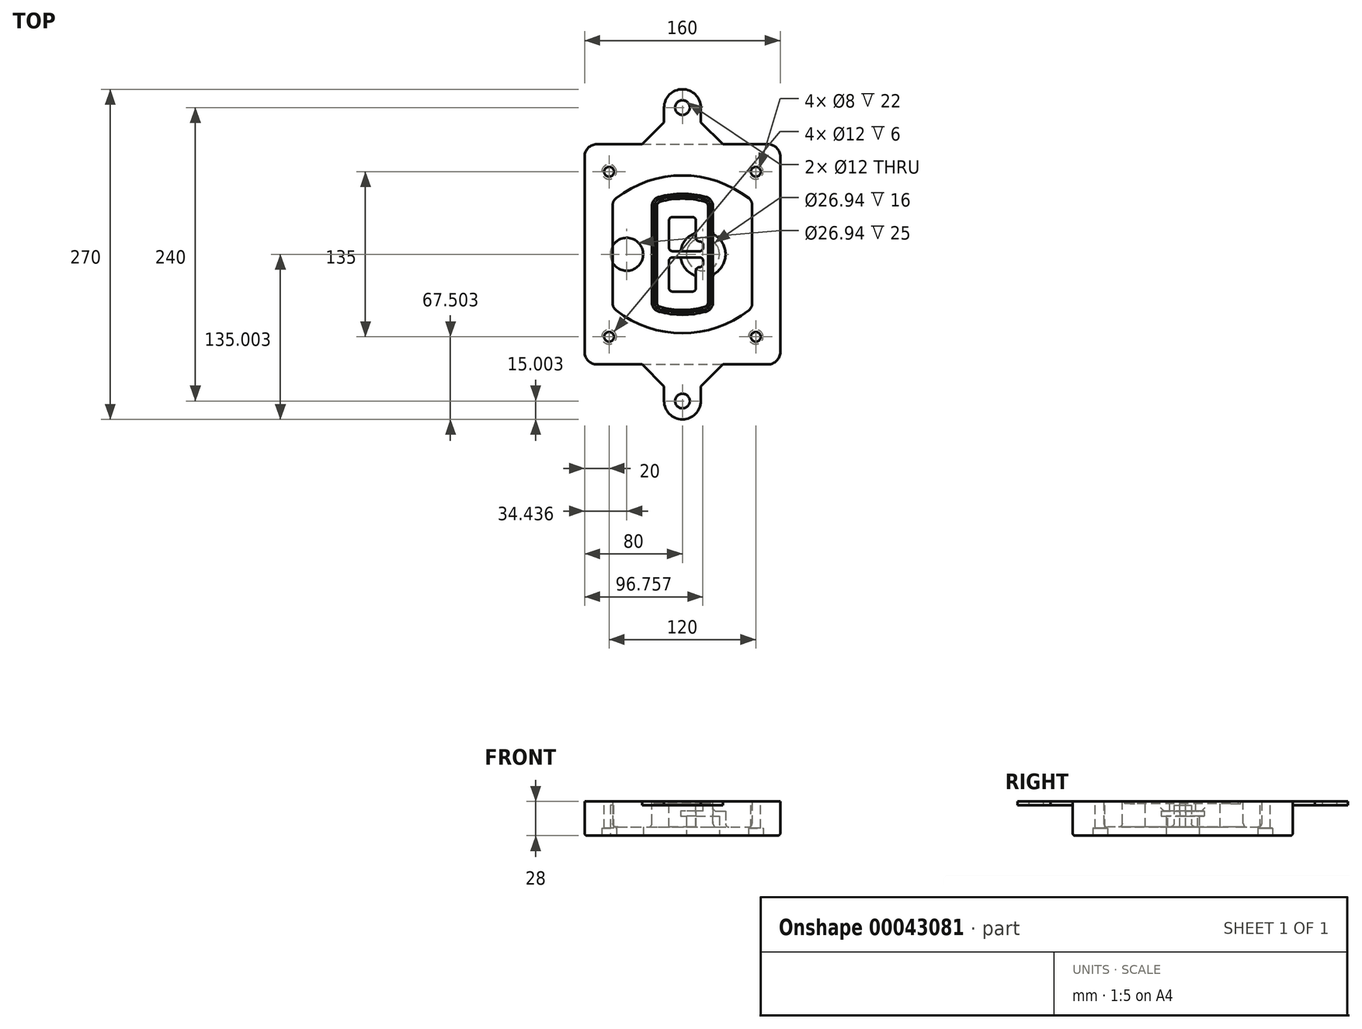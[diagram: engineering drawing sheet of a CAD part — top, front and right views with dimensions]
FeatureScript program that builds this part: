
annotation { "Feature Type Name" : "Feature", "Feature Type Description" : "" }
export const myFeature = defineFeature(function(context is Context, id is Id, definition is map)
    precondition{}
    {
        {
            var Q0;
            Q0=qCreatedBy(makeId("Top.planeOp"),FACE);
            var sketch = newSketch(context, id + "F0", { "sketchPlane" : qUnion([Q0])});
            skPoint(sketch, "E0.rect.middle", {"position": v(0, 0) * mm});
            skLineSegment(sketch, "E1.bottom", {"start": v(24.05, 28.38) * mm, "end": v(164.05, 28.38) * mm});
            skLineSegment(sketch, "E1.top", {"start": v(24.05, 208.38) * mm, "end": v(164.05, 208.38) * mm});
            skLineSegment(sketch, "E1.left", {"start": v(14.05, 38.38) * mm, "end": v(14.05, 198.38) * mm});
            skLineSegment(sketch, "E1.right", {"start": v(174.05, 38.38) * mm, "end": v(174.05, 198.38) * mm});
            skLineSegment(sketch, "E2", {"start": v(14.05, 208.38) * mm, "end": v(174.05, 28.38) * mm, "construction": true});
            skLineSegment(sketch, "E3", {"start": v(174.05, 208.38) * mm, "end": v(14.05, 28.38) * mm, "construction": true});
            skCircle(sketch, "E4", {"center": v(34.05, 185.88) * mm, "radius": 4 * mm});
            skCircle(sketch, "E5", {"center": v(154.05, 185.88) * mm, "radius": 4 * mm});
            skCircle(sketch, "E6", {"center": v(154.05, 50.88) * mm, "radius": 4 * mm});
            skCircle(sketch, "E7", {"center": v(34.05, 50.88) * mm, "radius": 4 * mm});
            skLineSegment(sketch, "E8", {"start": v(34.05, 185.88) * mm, "end": v(154.05, 185.88) * mm, "construction": true});
            skLineSegment(sketch, "E9", {"start": v(154.05, 185.88) * mm, "end": v(154.05, 50.88) * mm, "construction": true});
            skLineSegment(sketch, "E10", {"start": v(154.05, 50.88) * mm, "end": v(34.05, 50.88) * mm, "construction": true});
            skLineSegment(sketch, "E11", {"start": v(34.05, 50.88) * mm, "end": v(34.05, 185.88) * mm, "construction": true});
            skLineSegment(sketch, "E12", {"start": v(34.05, 158.68) * mm, "end": v(34.05, 78.09) * mm});
            skLineSegment(sketch, "E13", {"start": v(154.05, 158.68) * mm, "end": v(154.05, 78.09) * mm});
            skArc(sketch, "E14", {"start": v(150.2, 166.56) * mm, "mid": v(94.05, 185.88) * mm, "end": v(37.9, 166.56) * mm});
            skArc(sketch, "E15", {"start": v(37.9, 70.2) * mm, "mid": v(94.05, 50.88) * mm, "end": v(150.2, 70.2) * mm});
            skLineSegment(sketch, "E16", {"start": v(34.05, 118.38) * mm, "end": v(154.05, 118.38) * mm, "construction": true});
            skPoint(sketch, "E17.visualSharp", {"position": v(34.05, 73.38) * mm});
            skArc(sketch, "E17.filletArc", {"start": v(34.05, 78.09) * mm, "mid": v(35.06, 73.7) * mm, "end": v(37.9, 70.2) * mm});
            skPoint(sketch, "E18.visualSharp", {"position": v(34.05, 163.38) * mm});
            skArc(sketch, "E18.filletArc", {"start": v(37.9, 166.56) * mm, "mid": v(35.06, 163.06) * mm, "end": v(34.05, 158.68) * mm});
            skPoint(sketch, "E19.visualSharp", {"position": v(154.05, 163.38) * mm});
            skArc(sketch, "E19.filletArc", {"start": v(154.05, 158.68) * mm, "mid": v(153.04, 163.06) * mm, "end": v(150.2, 166.56) * mm});
            skPoint(sketch, "E20.visualSharp", {"position": v(154.05, 73.38) * mm});
            skArc(sketch, "E20.filletArc", {"start": v(150.2, 70.2) * mm, "mid": v(153.04, 73.7) * mm, "end": v(154.05, 78.09) * mm});
            skPoint(sketch, "E21.visualSharp", {"position": v(14.05, 208.38) * mm});
            skArc(sketch, "E21.filletArc", {"start": v(24.05, 208.38) * mm, "mid": v(16.98, 205.45) * mm, "end": v(14.05, 198.38) * mm});
            skPoint(sketch, "E22.visualSharp", {"position": v(174.05, 208.38) * mm});
            skArc(sketch, "E22.filletArc", {"start": v(174.05, 198.38) * mm, "mid": v(171.12, 205.45) * mm, "end": v(164.05, 208.38) * mm});
            skPoint(sketch, "E23.visualSharp", {"position": v(174.05, 28.38) * mm});
            skArc(sketch, "E23.filletArc", {"start": v(164.05, 28.38) * mm, "mid": v(171.12, 31.31) * mm, "end": v(174.05, 38.38) * mm});
            skPoint(sketch, "E24.visualSharp", {"position": v(14.05, 28.38) * mm});
            skArc(sketch, "E24.filletArc", {"start": v(14.05, 38.38) * mm, "mid": v(16.98, 31.31) * mm, "end": v(24.05, 28.38) * mm});
            skArc(sketch, "E25.0", {"start": v(151.05, 158.68) * mm, "mid": v(150.34, 161.75) * mm, "end": v(148.36, 164.2) * mm});
            skLineSegment(sketch, "E25.1", {"start": v(151.05, 158.68) * mm, "end": v(151.05, 78.09) * mm});
            skArc(sketch, "E25.2", {"start": v(148.36, 72.57) * mm, "mid": v(150.34, 75.02) * mm, "end": v(151.05, 78.09) * mm});
            skArc(sketch, "E25.3", {"start": v(39.74, 72.57) * mm, "mid": v(94.05, 53.88) * mm, "end": v(148.36, 72.57) * mm});
            skArc(sketch, "E25.4", {"start": v(37.05, 78.09) * mm, "mid": v(37.76, 75.02) * mm, "end": v(39.74, 72.57) * mm});
            skArc(sketch, "E25.5", {"start": v(148.36, 164.2) * mm, "mid": v(94.05, 182.88) * mm, "end": v(39.74, 164.2) * mm});
            skLineSegment(sketch, "E25.6", {"start": v(37.05, 158.68) * mm, "end": v(37.05, 78.09) * mm});
            skArc(sketch, "E25.7", {"start": v(39.74, 164.2) * mm, "mid": v(37.76, 161.75) * mm, "end": v(37.05, 158.68) * mm});
            skArc(sketch, "E26.0", {"start": v(35.43, 169.71) * mm, "mid": v(31.47, 164.82) * mm, "end": v(30.05, 158.68) * mm});
            skArc(sketch, "E26.1", {"start": v(152.67, 169.71) * mm, "mid": v(94.05, 189.88) * mm, "end": v(35.43, 169.71) * mm});
            skArc(sketch, "E26.2", {"start": v(158.05, 158.68) * mm, "mid": v(156.63, 164.82) * mm, "end": v(152.67, 169.71) * mm});
            skLineSegment(sketch, "E26.3", {"start": v(158.05, 158.68) * mm, "end": v(158.05, 78.09) * mm});
            skArc(sketch, "E26.4", {"start": v(152.67, 67.05) * mm, "mid": v(156.63, 71.95) * mm, "end": v(158.05, 78.09) * mm});
            skLineSegment(sketch, "E26.5", {"start": v(30.05, 158.68) * mm, "end": v(30.05, 78.09) * mm});
            skArc(sketch, "E26.6", {"start": v(35.43, 67.05) * mm, "mid": v(94.05, 46.88) * mm, "end": v(152.67, 67.05) * mm});
            skArc(sketch, "E26.7", {"start": v(30.05, 78.09) * mm, "mid": v(31.47, 71.95) * mm, "end": v(35.43, 67.05) * mm});
            skSolve(sketch);
        }
        {
            var Q0;
            Q0=makeQuery(id+"F0.imprint","IMPRINT",FACE,{"disambiguationData":[TD([[makeQuery(id+"F0.imprint","IMPRINT",EDGE,{"derivedFrom":sQuery(id+"F0.wireOp",EDGE,"E1.bottom")}),1.0]])]});
            var Q1;
            Q1=makeQuery(id+"F0.imprint","IMPRINT",FACE,{"disambiguationData":[TD([[makeQuery(id+"F0.imprint","IMPRINT",EDGE,{"derivedFrom":sQuery(id+"F0.wireOp",EDGE,"E12")}),1.0]])]});
            var Q2;
            Q2=makeQuery(id+"F0.imprint","IMPRINT",FACE,{"disambiguationData":[TD([[makeQuery(id+"F0.imprint","IMPRINT",EDGE,{"derivedFrom":sQuery(id+"F0.wireOp",EDGE,"E25.0")}),1.0]])]});
            var Q3;
            Q3=makeQuery(id+"F0.imprint","IMPRINT",FACE,{"disambiguationData":[TD([[makeQuery(id+"F0.imprint","IMPRINT",EDGE,{"derivedFrom":sQuery(id+"F0.wireOp",EDGE,"E12")}),-1.0]])]});
            extrude(context, id + "F1", {"entities" : qUnion([Q0, Q1, Q2, Q3]), "oppositeDirection" : true, "depth" : 25 * mm});
        }
        {
            var Q0;
            Q0=makeQuery(id+"F0.imprint","IMPRINT",FACE,{"disambiguationData":[TD([[makeQuery(id+"F0.imprint","IMPRINT",EDGE,{"derivedFrom":sQuery(id+"F0.wireOp",EDGE,"E12")}),1.0]])]});
            extrude(context, id + "F2", {"entities" : qUnion([Q0]), "operationType" : NewBodyOperationType.ADD, "depth" : 3 * mm});
        }
        {
            var Q0;
            Q0=makeQuery(id+"F0.imprint","IMPRINT",FACE,{"disambiguationData":[TD([[makeQuery(id+"F0.imprint","IMPRINT",EDGE,{"derivedFrom":sQuery(id+"F0.wireOp",EDGE,"E25.0")}),1.0]])]});
            extrude(context, id + "F3", {"entities" : qUnion([Q0]), "operationType" : NewBodyOperationType.REMOVE, "oppositeDirection" : true, "depth" : 18 * mm});
        }
        {
            var Q0;
            Q0=makeQuery(id+"F2.opExtrude","CAP_FACE",FACE,{"disambiguationData":[OSD([sQuery(id+"F0.wireOp",EDGE,"E12"),sQuery(id+"F0.wireOp",EDGE,"E13"),sQuery(id+"F0.wireOp",EDGE,"E14"),sQuery(id+"F0.wireOp",EDGE,"E15"),sQuery(id+"F0.wireOp",EDGE,"E17.filletArc"),sQuery(id+"F0.wireOp",EDGE,"E18.filletArc"),sQuery(id+"F0.wireOp",EDGE,"E19.filletArc"),sQuery(id+"F0.wireOp",EDGE,"E20.filletArc"),sQuery(id+"F0.wireOp",EDGE,"E25.0"),sQuery(id+"F0.wireOp",EDGE,"E25.1"),sQuery(id+"F0.wireOp",EDGE,"E25.2"),sQuery(id+"F0.wireOp",EDGE,"E25.3"),sQuery(id+"F0.wireOp",EDGE,"E25.4"),sQuery(id+"F0.wireOp",EDGE,"E25.5"),sQuery(id+"F0.wireOp",EDGE,"E25.6"),sQuery(id+"F0.wireOp",EDGE,"E25.7")])],"isStart":false});
            var sketch = newSketch(context, id + "F4", { "sketchPlane" : qUnion([Q0])});
            skArc(sketch, "E27.0", {"start": v(74.97, 71.41) * mm, "mid": v(94.05, 68.88) * mm, "end": v(113.13, 71.41) * mm});
            skArc(sketch, "E28.0", {"start": v(113.13, 165.35) * mm, "mid": v(94.05, 167.88) * mm, "end": v(74.97, 165.35) * mm});
            skLineSegment(sketch, "E29", {"start": v(69.05, 157.63) * mm, "end": v(69.05, 79.14) * mm});
            skLineSegment(sketch, "E30", {"start": v(119.05, 157.63) * mm, "end": v(119.05, 79.14) * mm});
            skLineSegment(sketch, "E31", {"start": v(69.05, 163.48) * mm, "end": v(119.05, 163.48) * mm, "construction": true});
            skLineSegment(sketch, "E32", {"start": v(69.05, 73.28) * mm, "end": v(119.05, 73.28) * mm, "construction": true});
            skPoint(sketch, "E33.visualSharp", {"position": v(69.05, 163.48) * mm});
            skArc(sketch, "E33.filletArc", {"start": v(74.97, 165.35) * mm, "mid": v(70.7, 162.5) * mm, "end": v(69.05, 157.63) * mm});
            skPoint(sketch, "E34.visualSharp", {"position": v(119.05, 163.48) * mm});
            skArc(sketch, "E34.filletArc", {"start": v(119.05, 157.63) * mm, "mid": v(117.4, 162.5) * mm, "end": v(113.13, 165.35) * mm});
            skPoint(sketch, "E35.visualSharp", {"position": v(119.05, 73.28) * mm});
            skArc(sketch, "E35.filletArc", {"start": v(113.13, 71.41) * mm, "mid": v(117.4, 74.27) * mm, "end": v(119.05, 79.14) * mm});
            skPoint(sketch, "E36.visualSharp", {"position": v(69.05, 73.28) * mm});
            skArc(sketch, "E36.filletArc", {"start": v(69.05, 79.14) * mm, "mid": v(70.7, 74.27) * mm, "end": v(74.97, 71.41) * mm});
            skArc(sketch, "E37.0", {"start": v(148.36, 164.2) * mm, "mid": v(94.05, 182.88) * mm, "end": v(39.74, 164.2) * mm});
            skArc(sketch, "E37.1", {"start": v(39.74, 164.2) * mm, "mid": v(37.76, 161.75) * mm, "end": v(37.05, 158.68) * mm});
            skLineSegment(sketch, "E37.2", {"start": v(37.05, 158.68) * mm, "end": v(37.05, 78.09) * mm});
            skArc(sketch, "E37.3", {"start": v(37.05, 78.09) * mm, "mid": v(37.76, 75.02) * mm, "end": v(39.74, 72.57) * mm});
            skArc(sketch, "E37.4", {"start": v(39.74, 72.57) * mm, "mid": v(94.05, 53.88) * mm, "end": v(148.36, 72.57) * mm});
            skArc(sketch, "E37.5", {"start": v(148.36, 72.57) * mm, "mid": v(150.34, 75.02) * mm, "end": v(151.05, 78.09) * mm});
            skLineSegment(sketch, "E37.6", {"start": v(151.05, 158.68) * mm, "end": v(151.05, 78.09) * mm});
            skArc(sketch, "E37.7", {"start": v(151.05, 158.68) * mm, "mid": v(150.34, 161.75) * mm, "end": v(148.36, 164.2) * mm});
            skLineSegment(sketch, "E38.0", {"start": v(117.05, 157.63) * mm, "end": v(117.05, 79.14) * mm});
            skArc(sketch, "E38.1", {"start": v(112.61, 73.34) * mm, "mid": v(115.81, 75.49) * mm, "end": v(117.05, 79.14) * mm});
            skArc(sketch, "E38.2", {"start": v(75.49, 73.34) * mm, "mid": v(94.05, 70.88) * mm, "end": v(112.61, 73.34) * mm});
            skArc(sketch, "E38.3", {"start": v(71.05, 79.14) * mm, "mid": v(72.29, 75.49) * mm, "end": v(75.49, 73.34) * mm});
            skLineSegment(sketch, "E38.4", {"start": v(71.05, 157.63) * mm, "end": v(71.05, 79.14) * mm});
            skArc(sketch, "E38.5", {"start": v(117.05, 157.63) * mm, "mid": v(115.81, 161.28) * mm, "end": v(112.61, 163.42) * mm});
            skArc(sketch, "E38.6", {"start": v(75.49, 163.42) * mm, "mid": v(72.29, 161.28) * mm, "end": v(71.05, 157.63) * mm});
            skArc(sketch, "E38.7", {"start": v(112.61, 163.42) * mm, "mid": v(94.05, 165.88) * mm, "end": v(75.49, 163.42) * mm});
            skArc(sketch, "E39.0", {"start": v(115.05, 157.63) * mm, "mid": v(114.23, 160.06) * mm, "end": v(112.1, 161.5) * mm});
            skLineSegment(sketch, "E39.1", {"start": v(115.05, 157.63) * mm, "end": v(115.05, 79.14) * mm});
            skArc(sketch, "E39.2", {"start": v(112.1, 75.27) * mm, "mid": v(114.23, 76.7) * mm, "end": v(115.05, 79.14) * mm});
            skArc(sketch, "E39.3", {"start": v(76, 75.27) * mm, "mid": v(94.05, 72.88) * mm, "end": v(112.1, 75.27) * mm});
            skArc(sketch, "E39.4", {"start": v(73.05, 79.14) * mm, "mid": v(73.87, 76.7) * mm, "end": v(76, 75.27) * mm});
            skArc(sketch, "E39.5", {"start": v(112.1, 161.5) * mm, "mid": v(94.05, 163.88) * mm, "end": v(76, 161.5) * mm});
            skLineSegment(sketch, "E39.6", {"start": v(73.05, 157.63) * mm, "end": v(73.05, 79.14) * mm});
            skArc(sketch, "E39.7", {"start": v(76, 161.5) * mm, "mid": v(73.87, 160.06) * mm, "end": v(73.05, 157.63) * mm});
            skLineSegment(sketch, "E40", {"start": v(69.05, 118.38) * mm, "end": v(119.05, 118.38) * mm, "construction": true});
            skLineSegment(sketch, "E41", {"start": v(83.05, 123.88) * mm, "end": v(83.05, 145.88) * mm});
            skLineSegment(sketch, "E42", {"start": v(86.05, 148.88) * mm, "end": v(102.05, 148.88) * mm});
            skLineSegment(sketch, "E43", {"start": v(105.05, 145.88) * mm, "end": v(105.05, 131.88) * mm});
            skLineSegment(sketch, "E44", {"start": v(108.05, 128.88) * mm, "end": v(108.05, 128.88) * mm});
            skLineSegment(sketch, "E45", {"start": v(111.05, 125.88) * mm, "end": v(111.05, 123.88) * mm});
            skLineSegment(sketch, "E46", {"start": v(108.05, 120.88) * mm, "end": v(86.05, 120.88) * mm});
            skPoint(sketch, "E47.visualSharp", {"position": v(83.05, 148.88) * mm});
            skArc(sketch, "E47.filletArc", {"start": v(86.05, 148.88) * mm, "mid": v(83.93, 148) * mm, "end": v(83.05, 145.88) * mm});
            skPoint(sketch, "E48.visualSharp", {"position": v(105.05, 148.88) * mm});
            skArc(sketch, "E48.filletArc", {"start": v(105.05, 145.88) * mm, "mid": v(104.17, 148) * mm, "end": v(102.05, 148.88) * mm});
            skPoint(sketch, "E49.visualSharp", {"position": v(105.05, 128.88) * mm});
            skArc(sketch, "E49.filletArc", {"start": v(105.05, 131.88) * mm, "mid": v(105.93, 129.76) * mm, "end": v(108.05, 128.88) * mm});
            skPoint(sketch, "E50.visualSharp", {"position": v(111.05, 128.88) * mm});
            skArc(sketch, "E50.filletArc", {"start": v(111.05, 125.88) * mm, "mid": v(110.17, 128) * mm, "end": v(108.05, 128.88) * mm});
            skPoint(sketch, "E51.visualSharp", {"position": v(111.05, 120.88) * mm});
            skArc(sketch, "E51.filletArc", {"start": v(108.05, 120.88) * mm, "mid": v(110.17, 121.76) * mm, "end": v(111.05, 123.88) * mm});
            skPoint(sketch, "E52.visualSharp", {"position": v(83.05, 120.88) * mm});
            skArc(sketch, "E52.filletArc", {"start": v(83.05, 123.88) * mm, "mid": v(83.93, 121.76) * mm, "end": v(86.05, 120.88) * mm});
            skLineSegment(sketch, "E53.0.MirrorCS", {"start": v(108.05, 115.88) * mm, "end": v(86.05, 115.88) * mm});
            skArc(sketch, "E54.0.MirrorCS", {"start": v(83.05, 112.88) * mm, "mid": v(83.93, 115) * mm, "end": v(86.05, 115.88) * mm});
            skLineSegment(sketch, "E55.0.MirrorCS", {"start": v(83.05, 112.88) * mm, "end": v(83.05, 90.88) * mm});
            skArc(sketch, "E56.0.MirrorCS", {"start": v(86.05, 87.88) * mm, "mid": v(83.93, 88.76) * mm, "end": v(83.05, 90.88) * mm});
            skLineSegment(sketch, "E57.0.MirrorCS", {"start": v(86.05, 87.88) * mm, "end": v(102.05, 87.88) * mm});
            skArc(sketch, "E58.0.MirrorCS", {"start": v(105.05, 90.88) * mm, "mid": v(104.17, 88.76) * mm, "end": v(102.05, 87.88) * mm});
            skLineSegment(sketch, "E59.0.MirrorCS", {"start": v(105.05, 90.88) * mm, "end": v(105.05, 104.88) * mm});
            skArc(sketch, "E60.0.MirrorCS", {"start": v(105.05, 104.88) * mm, "mid": v(105.93, 107) * mm, "end": v(108.05, 107.88) * mm});
            skArc(sketch, "E61.0.MirrorCS", {"start": v(111.05, 110.88) * mm, "mid": v(110.17, 108.76) * mm, "end": v(108.05, 107.88) * mm});
            skLineSegment(sketch, "E62.0.MirrorCS", {"start": v(111.05, 110.88) * mm, "end": v(111.05, 112.88) * mm});
            skArc(sketch, "E63.0.MirrorCS", {"start": v(108.05, 115.88) * mm, "mid": v(110.17, 115) * mm, "end": v(111.05, 112.88) * mm});
            skSolve(sketch);
        }
        {
            var Q0;
            Q0=makeQuery(id+"F4.imprint","IMPRINT",FACE,{"disambiguationData":[TD([[makeQuery(id+"F4.imprint","IMPRINT",EDGE,{"derivedFrom":sQuery(id+"F4.wireOp",EDGE,"E27.0")}),1.0]])]});
            var Q1;
            Q1=makeQuery(id+"F4.imprint","IMPRINT",FACE,{"disambiguationData":[TD([[makeQuery(id+"F4.imprint","IMPRINT",EDGE,{"derivedFrom":sQuery(id+"F4.wireOp",EDGE,"E38.0")}),-1.0]])]});
            var Q2;
            Q2=makeQuery(id+"F4.imprint","IMPRINT",FACE,{"disambiguationData":[TD([[makeQuery(id+"F4.imprint","IMPRINT",EDGE,{"derivedFrom":sQuery(id+"F4.wireOp",EDGE,"E39.0")}),1.0]])]});
            extrude(context, id + "F5", {"entities" : qUnion([Q0, Q1, Q2]), "operationType" : NewBodyOperationType.ADD, "endBound" : BoundingType.UP_TO_NEXT, "oppositeDirection" : true, "depth" : 25 * mm});
        }
        {
            var Q0;
            Q0=makeQuery(id+"F4.imprint","IMPRINT",FACE,{"disambiguationData":[TD([[makeQuery(id+"F4.imprint","IMPRINT",EDGE,{"derivedFrom":sQuery(id+"F4.wireOp",EDGE,"E38.0")}),-1.0]])]});
            extrude(context, id + "F6", {"entities" : qUnion([Q0]), "operationType" : NewBodyOperationType.REMOVE, "oppositeDirection" : true, "depth" : 2 * mm});
        }
        {
            var Q0;
            Q0=makeQuery(id+"F1.opExtrude","CAP_FACE",FACE,{"disambiguationData":[OSD([sQuery(id+"F0.wireOp",EDGE,"E1.bottom"),sQuery(id+"F0.wireOp",EDGE,"E1.top"),sQuery(id+"F0.wireOp",EDGE,"E1.left"),sQuery(id+"F0.wireOp",EDGE,"E1.right"),sQuery(id+"F0.wireOp",EDGE,"E4"),sQuery(id+"F0.wireOp",EDGE,"E5"),sQuery(id+"F0.wireOp",EDGE,"E6"),sQuery(id+"F0.wireOp",EDGE,"E7"),sQuery(id+"F0.wireOp",EDGE,"E21.filletArc"),sQuery(id+"F0.wireOp",EDGE,"E22.filletArc"),sQuery(id+"F0.wireOp",EDGE,"E23.filletArc"),sQuery(id+"F0.wireOp",EDGE,"E24.filletArc")])],"isStart":false});
            var sketch = newSketch(context, id + "F7", { "sketchPlane" : qUnion([Q0])});
            skCircle(sketch, "E64", {"center": v(110.8, -118.38) * mm, "radius": 13.47 * mm});
            skCircle(sketch, "E65", {"center": v(48.49, -118.38) * mm, "radius": 13.47 * mm});
            skLineSegment(sketch, "E66", {"start": v(174.05, -118.38) * mm, "end": v(14.05, -118.38) * mm});
            skCircle(sketch, "E67", {"center": v(110.8, -118.38) * mm, "radius": 18.47 * mm});
            skCircle(sketch, "E68", {"center": v(154.05, -185.88) * mm, "radius": 6 * mm});
            skCircle(sketch, "E69", {"center": v(34.05, -185.88) * mm, "radius": 6 * mm});
            skCircle(sketch, "E70", {"center": v(34.05, -50.88) * mm, "radius": 6 * mm});
            skCircle(sketch, "E71", {"center": v(154.05, -50.88) * mm, "radius": 6 * mm});
            skSolve(sketch);
        }
        {
            var Q0;
            {var subQ1=sQuery(id+"F7.wireOp",EDGE,"E66");var subQ4=sQuery(id+"F7.wireOp",EDGE,"E64");var subQ6=makeQuery(id+"F7.imprint","INTERSECT",VERTEX,{"disambiguationData":[OD(0.0)],"derivedFrom":[subQ4,subQ1]});Q0=makeQuery(id+"F7.imprint","IMPRINT",FACE,{"disambiguationData":[TD([[makeQuery(id+"F7.imprint","IMPRINT",EDGE,{"disambiguationData":[TD([[subQ6,-1.0]])],"derivedFrom":subQ4}),-1.0]])]});}
            var Q1;
            {var subQ0=sQuery(id+"F7.wireOp",EDGE,"E66");var subQ1=sQuery(id+"F7.wireOp",EDGE,"E64");var subQ3=makeQuery(id+"F7.imprint","INTERSECT",VERTEX,{"disambiguationData":[OD(0.0)],"derivedFrom":[subQ1,subQ0]});Q1=makeQuery(id+"F7.imprint","IMPRINT",FACE,{"disambiguationData":[TD([[makeQuery(id+"F7.imprint","IMPRINT",EDGE,{"disambiguationData":[TD([[subQ3,-1.0]])],"derivedFrom":subQ1}),1.0]])]});}
            var Q2;
            {var subQ0=sQuery(id+"F7.wireOp",EDGE,"E66");var subQ1=sQuery(id+"F7.wireOp",EDGE,"E64");var subQ3=makeQuery(id+"F7.imprint","INTERSECT",VERTEX,{"disambiguationData":[OD(0.0)],"derivedFrom":[subQ1,subQ0]});Q2=makeQuery(id+"F7.imprint","IMPRINT",FACE,{"disambiguationData":[TD([[makeQuery(id+"F7.imprint","IMPRINT",EDGE,{"disambiguationData":[TD([[subQ3,1.0]])],"derivedFrom":subQ1}),1.0]])]});}
            var Q3;
            {var subQ1=sQuery(id+"F7.wireOp",EDGE,"E66");var subQ4=sQuery(id+"F7.wireOp",EDGE,"E64");var subQ6=makeQuery(id+"F7.imprint","INTERSECT",VERTEX,{"disambiguationData":[OD(0.0)],"derivedFrom":[subQ4,subQ1]});Q3=makeQuery(id+"F7.imprint","IMPRINT",FACE,{"disambiguationData":[TD([[makeQuery(id+"F7.imprint","IMPRINT",EDGE,{"disambiguationData":[TD([[subQ6,1.0]])],"derivedFrom":subQ4}),-1.0]])]});}
            extrude(context, id + "F8", {"entities" : qUnion([Q0, Q1, Q2, Q3]), "operationType" : NewBodyOperationType.ADD, "oppositeDirection" : true, "depth" : 20 * mm});
        }
        {
            var Q0;
            {var subQ0=sQuery(id+"F7.wireOp",EDGE,"E66");var subQ1=sQuery(id+"F7.wireOp",EDGE,"E64");var subQ3=makeQuery(id+"F7.imprint","INTERSECT",VERTEX,{"disambiguationData":[OD(0.0)],"derivedFrom":[subQ1,subQ0]});Q0=makeQuery(id+"F7.imprint","IMPRINT",FACE,{"disambiguationData":[TD([[makeQuery(id+"F7.imprint","IMPRINT",EDGE,{"disambiguationData":[TD([[subQ3,-1.0]])],"derivedFrom":subQ1}),1.0]])]});}
            var Q1;
            {var subQ0=sQuery(id+"F7.wireOp",EDGE,"E66");var subQ1=sQuery(id+"F7.wireOp",EDGE,"E64");var subQ3=makeQuery(id+"F7.imprint","INTERSECT",VERTEX,{"disambiguationData":[OD(0.0)],"derivedFrom":[subQ1,subQ0]});Q1=makeQuery(id+"F7.imprint","IMPRINT",FACE,{"disambiguationData":[TD([[makeQuery(id+"F7.imprint","IMPRINT",EDGE,{"disambiguationData":[TD([[subQ3,1.0]])],"derivedFrom":subQ1}),1.0]])]});}
            extrude(context, id + "F9", {"entities" : qUnion([Q0, Q1]), "operationType" : NewBodyOperationType.REMOVE, "oppositeDirection" : true, "depth" : 16 * mm});
        }
        {
            var Q0;
            {var subQ0=sQuery(id+"F7.wireOp",EDGE,"E66");var subQ1=sQuery(id+"F7.wireOp",EDGE,"E65");var subQ3=makeQuery(id+"F7.imprint","INTERSECT",VERTEX,{"disambiguationData":[OD(0.0)],"derivedFrom":[subQ1,subQ0]});Q0=makeQuery(id+"F7.imprint","IMPRINT",FACE,{"disambiguationData":[TD([[makeQuery(id+"F7.imprint","IMPRINT",EDGE,{"disambiguationData":[TD([[subQ3,-1.0]])],"derivedFrom":subQ1}),1.0]])]});}
            var Q1;
            {var subQ0=sQuery(id+"F7.wireOp",EDGE,"E66");var subQ1=sQuery(id+"F7.wireOp",EDGE,"E65");var subQ3=makeQuery(id+"F7.imprint","INTERSECT",VERTEX,{"disambiguationData":[OD(0.0)],"derivedFrom":[subQ1,subQ0]});Q1=makeQuery(id+"F7.imprint","IMPRINT",FACE,{"disambiguationData":[TD([[makeQuery(id+"F7.imprint","IMPRINT",EDGE,{"disambiguationData":[TD([[subQ3,1.0]])],"derivedFrom":subQ1}),1.0]])]});}
            extrude(context, id + "F10", {"entities" : qUnion([Q0, Q1]), "operationType" : NewBodyOperationType.REMOVE, "oppositeDirection" : true, "depth" : 25 * mm});
        }
        {
            var Q0;
            Q0=makeQuery(id+"F7.imprint","IMPRINT",FACE,{"disambiguationData":[TD([[makeQuery(id+"F7.imprint","IMPRINT",EDGE,{"derivedFrom":sQuery(id+"F7.wireOp",EDGE,"E68")}),1.0]])]});
            var Q1;
            Q1=makeQuery(id+"F7.imprint","IMPRINT",FACE,{"disambiguationData":[TD([[makeQuery(id+"F7.imprint","IMPRINT",EDGE,{"derivedFrom":makeQuery(id+"F1.opExtrude","CAP_EDGE",EDGE,{"disambiguationData":[OSD([sQuery(id+"F0.wireOp",EDGE,"E5")])],"isStart":false})}),-1.0]])]});
            var Q2;
            Q2=makeQuery(id+"F7.imprint","IMPRINT",FACE,{"disambiguationData":[TD([[makeQuery(id+"F7.imprint","IMPRINT",EDGE,{"derivedFrom":sQuery(id+"F7.wireOp",EDGE,"E69")}),1.0]])]});
            var Q3;
            Q3=makeQuery(id+"F7.imprint","IMPRINT",FACE,{"disambiguationData":[TD([[makeQuery(id+"F7.imprint","IMPRINT",EDGE,{"derivedFrom":makeQuery(id+"F1.opExtrude","CAP_EDGE",EDGE,{"disambiguationData":[OSD([sQuery(id+"F0.wireOp",EDGE,"E4")])],"isStart":false})}),-1.0]])]});
            var Q4;
            Q4=makeQuery(id+"F7.imprint","IMPRINT",FACE,{"disambiguationData":[TD([[makeQuery(id+"F7.imprint","IMPRINT",EDGE,{"derivedFrom":sQuery(id+"F7.wireOp",EDGE,"E70")}),1.0]])]});
            var Q5;
            Q5=makeQuery(id+"F7.imprint","IMPRINT",FACE,{"disambiguationData":[TD([[makeQuery(id+"F7.imprint","IMPRINT",EDGE,{"derivedFrom":makeQuery(id+"F1.opExtrude","CAP_EDGE",EDGE,{"disambiguationData":[OSD([sQuery(id+"F0.wireOp",EDGE,"E7")])],"isStart":false})}),-1.0]])]});
            var Q6;
            Q6=makeQuery(id+"F7.imprint","IMPRINT",FACE,{"disambiguationData":[TD([[makeQuery(id+"F7.imprint","IMPRINT",EDGE,{"derivedFrom":sQuery(id+"F7.wireOp",EDGE,"E71")}),1.0]])]});
            var Q7;
            Q7=makeQuery(id+"F7.imprint","IMPRINT",FACE,{"disambiguationData":[TD([[makeQuery(id+"F7.imprint","IMPRINT",EDGE,{"derivedFrom":makeQuery(id+"F1.opExtrude","CAP_EDGE",EDGE,{"disambiguationData":[OSD([sQuery(id+"F0.wireOp",EDGE,"E6")])],"isStart":false})}),-1.0]])]});
            extrude(context, id + "F11", {"entities" : qUnion([Q0, Q1, Q2, Q3, Q4, Q5, Q6, Q7]), "operationType" : NewBodyOperationType.REMOVE, "oppositeDirection" : true, "depth" : 6 * mm});
        }
        {
            var Q0;
            Q0=makeQuery(id+"F9.boolean.opBoolean","COPY",FACE,{"derivedFrom":makeQuery(id+"F9.opExtrude","CAP_FACE",FACE,{"disambiguationData":[OSD([sQuery(id+"F7.wireOp",EDGE,"E64")])],"isStart":false})});
            var sketch = newSketch(context, id + "F12", { "sketchPlane" : qUnion([Q0])});
            skArc(sketch, "E72.0", {"start": v(105.05, -100.83) * mm, "mid": v(96.62, -106.56) * mm, "end": v(92.5, -115.88) * mm});
            skArc(sketch, "E72.1", {"start": v(92.5, -120.88) * mm, "mid": v(96.62, -130.2) * mm, "end": v(105.05, -135.93) * mm});
            skLineSegment(sketch, "E73", {"start": v(92.5, -120.88) * mm, "end": v(108.05, -120.88) * mm});
            skLineSegment(sketch, "E74.0", {"start": v(108.05, -115.88) * mm, "end": v(92.5, -115.88) * mm});
            skArc(sketch, "E74.1", {"start": v(108.05, -115.88) * mm, "mid": v(110.17, -115) * mm, "end": v(111.05, -112.88) * mm});
            skLineSegment(sketch, "E74.2", {"start": v(111.05, -110.88) * mm, "end": v(111.05, -112.88) * mm});
            skArc(sketch, "E74.3", {"start": v(111.05, -110.88) * mm, "mid": v(110.17, -108.76) * mm, "end": v(108.05, -107.88) * mm});
            skArc(sketch, "E74.4", {"start": v(105.05, -104.88) * mm, "mid": v(105.93, -107) * mm, "end": v(108.05, -107.88) * mm});
            skLineSegment(sketch, "E74.5", {"start": v(105.05, -100.83) * mm, "end": v(105.05, -104.88) * mm});
            skLineSegment(sketch, "E74.7", {"start": v(108.05, -120.88) * mm, "end": v(92.5, -120.88) * mm});
            skArc(sketch, "E74.8", {"start": v(108.05, -120.88) * mm, "mid": v(110.17, -121.76) * mm, "end": v(111.05, -123.88) * mm});
            skLineSegment(sketch, "E74.9", {"start": v(111.05, -125.88) * mm, "end": v(111.05, -123.88) * mm});
            skArc(sketch, "E74.10", {"start": v(111.05, -125.88) * mm, "mid": v(110.17, -128) * mm, "end": v(108.05, -128.88) * mm});
            skArc(sketch, "E74.11", {"start": v(105.05, -131.88) * mm, "mid": v(105.93, -129.76) * mm, "end": v(108.05, -128.88) * mm});
            skLineSegment(sketch, "E74.12", {"start": v(105.05, -135.93) * mm, "end": v(105.05, -131.88) * mm});
            skPoint(sketch, "E75.orphan", {"position": v(105.05, -145.88) * mm});
            skPoint(sketch, "E76.orphan", {"position": v(86.05, -120.88) * mm});
            skPoint(sketch, "E77.orphan", {"position": v(86.05, -115.88) * mm});
            skPoint(sketch, "E78.orphan", {"position": v(105.05, -90.88) * mm});
            skSolve(sketch);
        }
        {
            var Q0;
            {var subQ7=sQuery(id+"F12.wireOp",EDGE,"E72.0");var subQ14=sQuery(id+"F12.wireOp",EDGE,"E72.1");var subQ16=sQuery(id+"F12.wireOp",EDGE,"E74.1");var subQ18=sQuery(id+"F12.wireOp",EDGE,"E74.8");Q0=qUnion([makeQuery(id+"F12.imprint","IMPRINT",FACE,{"disambiguationData":[TD([[makeQuery(id+"F12.imprint","IMPRINT",EDGE,{"derivedFrom":subQ7}),1.0]])]}),makeQuery(id+"F12.imprint","IMPRINT",FACE,{"disambiguationData":[TD([[makeQuery(id+"F12.imprint","IMPRINT",EDGE,{"derivedFrom":subQ14}),1.0]])]}),makeQuery(id+"F12.imprint","IMPRINT",FACE,{"disambiguationData":[TD([[makeQuery(id+"F12.imprint","IMPRINT",EDGE,{"derivedFrom":subQ16}),1.0]])]}),makeQuery(id+"F12.imprint","IMPRINT",FACE,{"disambiguationData":[TD([[makeQuery(id+"F12.imprint","IMPRINT",EDGE,{"derivedFrom":subQ18}),-1.0]])]})]);}
            var Q1;
            Q1=makeQuery(id+"F5.boolean.opBoolean","SPLIT",FACE,{"disambiguationData":[TD([makeQuery(id+"F5.opExtrude","SWEPT_FACE",FACE,{"disambiguationData":[OSD([sQuery(id+"F4.wireOp",EDGE,"E41")])]})])],"derivedFrom":makeQuery(id+"F3.boolean.opBoolean","COPY",FACE,{"derivedFrom":makeQuery(id+"F3.opExtrude","CAP_FACE",FACE,{"disambiguationData":[OSD([sQuery(id+"F0.wireOp",EDGE,"E25.0"),sQuery(id+"F0.wireOp",EDGE,"E25.1"),sQuery(id+"F0.wireOp",EDGE,"E25.2"),sQuery(id+"F0.wireOp",EDGE,"E25.3"),sQuery(id+"F0.wireOp",EDGE,"E25.4"),sQuery(id+"F0.wireOp",EDGE,"E25.5"),sQuery(id+"F0.wireOp",EDGE,"E25.6"),sQuery(id+"F0.wireOp",EDGE,"E25.7")])],"isStart":false})})});
            extrude(context, id + "F13", {"entities" : qUnion([Q0]), "operationType" : NewBodyOperationType.REMOVE, "endBound" : BoundingType.UP_TO_SURFACE, "endBoundEntityFace" : qUnion([Q1]), "depth" : 25 * mm});
        }
        {
            var Q0;
            Q0=makeQuery(id+"F3.boolean.opBoolean","COPY",EDGE,{"derivedFrom":makeQuery(id+"F3.opExtrude","CAP_EDGE",EDGE,{"disambiguationData":[OSD([sQuery(id+"F0.wireOp",EDGE,"E25.6")])],"isStart":false})});
            var Q1;
            Q1=makeQuery(id+"F8.boolean.opBoolean","INTERSECT",EDGE,{"derivedFrom":[makeQuery(id+"F5.opExtrude","SWEPT_FACE",FACE,{"disambiguationData":[OSD([sQuery(id+"F4.wireOp",EDGE,"E30")])]}),makeQuery(id+"F8.opExtrude","CAP_FACE",FACE,{"disambiguationData":[OSD([sQuery(id+"F7.wireOp",EDGE,"E67")])],"isStart":false})]});
            var Q2;
            Q2=makeQuery(id+"F8.boolean.opBoolean","INTERSECT",EDGE,{"disambiguationData":[OD(1.0)],"derivedFrom":[makeQuery(id+"F5.opExtrude","SWEPT_FACE",FACE,{"disambiguationData":[OSD([sQuery(id+"F4.wireOp",EDGE,"E30")])]}),makeQuery(id+"F8.opExtrude","SWEPT_FACE",FACE,{"disambiguationData":[OSD([sQuery(id+"F7.wireOp",EDGE,"E67")])]})]});
            var Q3;
            {var subQ0=sQuery(id+"F4.wireOp",EDGE,"E30");Q3=makeQuery(id+"F8.boolean.opBoolean","SPLIT",EDGE,{"disambiguationData":[TD([makeQuery(id+"F5.opExtrude","SWEPT_FACE",FACE,{"disambiguationData":[OSD([sQuery(id+"F4.wireOp",EDGE,"E35.filletArc")])]})])],"derivedFrom":makeQuery(id+"F5.opExtrude","CAP_EDGE",EDGE,{"disambiguationData":[OSD([subQ0])],"isStart":false})});}
            var Q4;
            {var subQ0=sQuery(id+"F0.wireOp",EDGE,"E25.7");var subQ1=sQuery(id+"F0.wireOp",EDGE,"E25.1");var subQ2=sQuery(id+"F0.wireOp",EDGE,"E25.6");var subQ3=sQuery(id+"F0.wireOp",EDGE,"E25.5");var subQ4=sQuery(id+"F0.wireOp",EDGE,"E25.4");var subQ5=sQuery(id+"F0.wireOp",EDGE,"E25.0");var subQ6=sQuery(id+"F0.wireOp",EDGE,"E25.2");var subQ7=sQuery(id+"F0.wireOp",EDGE,"E25.3");Q4=makeQuery(id+"F8.boolean.opBoolean","INTERSECT",EDGE,{"derivedFrom":[makeQuery(id+"F5.boolean.opBoolean","SPLIT",FACE,{"disambiguationData":[TD([makeQuery(id+"F2.opExtrude","SWEPT_FACE",FACE,{"disambiguationData":[OSD([subQ5])]})])],"derivedFrom":makeQuery(id+"F3.boolean.opBoolean","COPY",FACE,{"derivedFrom":makeQuery(id+"F3.opExtrude","CAP_FACE",FACE,{"disambiguationData":[OSD([subQ5,subQ1,subQ6,subQ7,subQ4,subQ3,subQ2,subQ0])],"isStart":false})})}),makeQuery(id+"F8.opExtrude","SWEPT_FACE",FACE,{"disambiguationData":[OSD([sQuery(id+"F7.wireOp",EDGE,"E67")])]})]});}
            var Q5;
            Q5=makeQuery(id+"F8.boolean.opBoolean","INTERSECT",EDGE,{"disambiguationData":[OD(0.0)],"derivedFrom":[makeQuery(id+"F5.opExtrude","SWEPT_FACE",FACE,{"disambiguationData":[OSD([sQuery(id+"F4.wireOp",EDGE,"E30")])]}),makeQuery(id+"F8.opExtrude","SWEPT_FACE",FACE,{"disambiguationData":[OSD([sQuery(id+"F7.wireOp",EDGE,"E67")])]})]});
            fillet(context, id + "F14", {"entities" : qUnion([Q0, Q1, Q2, Q3, Q4, Q5]), "radius" : 3 * mm, "tangentPropagation" : true, "allowEdgeOverflow" : false});
        }
        {
            var Q0;
            Q0=makeQuery(id+"F1.opExtrude","CAP_EDGE",EDGE,{"disambiguationData":[OSD([sQuery(id+"F0.wireOp",EDGE,"E1.bottom")])],"isStart":false});
            fillet(context, id + "F15", {"entities" : qUnion([Q0]), "radius" : 2 * mm, "tangentPropagation" : true, "allowEdgeOverflow" : false});
        }
        {
            var Q0;
            {var subQ0=sQuery(id+"F0.wireOp",EDGE,"E1.bottom");var subQ1=sQuery(id+"F0.wireOp",EDGE,"E1.top");var subQ2=sQuery(id+"F0.wireOp",EDGE,"E1.left");var subQ3=sQuery(id+"F0.wireOp",EDGE,"E1.right");var subQ4=sQuery(id+"F0.wireOp",EDGE,"E4");var subQ5=sQuery(id+"F0.wireOp",EDGE,"E5");var subQ6=sQuery(id+"F0.wireOp",EDGE,"E6");var subQ7=sQuery(id+"F0.wireOp",EDGE,"E7");var subQ8=sQuery(id+"F0.wireOp",EDGE,"E21.filletArc");var subQ9=sQuery(id+"F0.wireOp",EDGE,"E22.filletArc");var subQ10=sQuery(id+"F0.wireOp",EDGE,"E23.filletArc");var subQ11=sQuery(id+"F0.wireOp",EDGE,"E24.filletArc");Q0=makeQuery(id+"F2.boolean.opBoolean","SPLIT",FACE,{"disambiguationData":[TD([makeQuery(id+"F1.opExtrude","SWEPT_FACE",FACE,{"disambiguationData":[OSD([subQ0])]})])],"derivedFrom":makeQuery(id+"F1.opExtrude","CAP_FACE",FACE,{"disambiguationData":[OSD([subQ0,subQ1,subQ2,subQ3,subQ4,subQ5,subQ6,subQ7,subQ8,subQ9,subQ10,subQ11])],"isStart":true})});}
            var sketch = newSketch(context, id + "F16", { "sketchPlane" : qUnion([Q0])});
            skLineSegment(sketch, "E79", {"start": v(94.05, 208.38) * mm, "end": v(94.05, 238.38) * mm, "construction": true});
            skPoint(sketch, "E79.endSnap0", {"position": v(94.05, 208.38) * mm});
            skCircle(sketch, "E80", {"center": v(94.05, 238.38) * mm, "radius": 6 * mm});
            skArc(sketch, "E81", {"start": v(109.05, 238.38) * mm, "mid": v(94.05, 253.38) * mm, "end": v(79.05, 238.38) * mm});
            skLineSegment(sketch, "E82", {"start": v(79.05, 238.38) * mm, "end": v(79.05, 226.38) * mm});
            skLineSegment(sketch, "E83", {"start": v(79.05, 226.38) * mm, "end": v(61.05, 208.38) * mm});
            skLineSegment(sketch, "E84", {"start": v(109.05, 238.38) * mm, "end": v(109.05, 226.38) * mm});
            skLineSegment(sketch, "E85", {"start": v(109.05, 226.38) * mm, "end": v(127.05, 208.38) * mm});
            skLineSegment(sketch, "E86", {"start": v(14.05, 118.38) * mm, "end": v(174.05, 118.38) * mm, "construction": true});
            skLineSegment(sketch, "E87.MirrorCS", {"start": v(109.05, 10.38) * mm, "end": v(127.05, 28.38) * mm});
            skLineSegment(sketch, "E88.MirrorCS", {"start": v(79.05, 10.38) * mm, "end": v(61.05, 28.38) * mm});
            skArc(sketch, "E89.MirrorCS", {"start": v(109.05, -1.62) * mm, "mid": v(94.05, -16.62) * mm, "end": v(79.05, -1.62) * mm});
            skLineSegment(sketch, "E90.MirrorCS", {"start": v(79.05, -1.62) * mm, "end": v(79.05, 10.38) * mm});
            skLineSegment(sketch, "E91.MirrorCS", {"start": v(109.05, -1.62) * mm, "end": v(109.05, 10.38) * mm});
            skCircle(sketch, "E92.MirrorC", {"center": v(94.05, -1.62) * mm, "radius": 6 * mm});
            skLineSegment(sketch, "E93.MirrorCS", {"start": v(94.05, 28.38) * mm, "end": v(94.05, -1.62) * mm, "construction": true});
            skSolve(sketch);
        }
        {
            var Q0;
            Q0=makeQuery(id+"F16.imprint","IMPRINT",FACE,{"disambiguationData":[TD([[makeQuery(id+"F16.imprint","IMPRINT",EDGE,{"derivedFrom":sQuery(id+"F16.wireOp",EDGE,"E80")}),-1.0]])]});
            var Q1;
            {var subQ1=sQuery(id+"F16.wireOp",EDGE,"E87.MirrorCS");Q1=makeQuery(id+"F16.imprint","IMPRINT",FACE,{"disambiguationData":[TD([[makeQuery(id+"F16.imprint","IMPRINT",EDGE,{"derivedFrom":subQ1}),1.0]])]});}
            var Q2;
            Q2=makeQuery(id+"F16.imprint","IMPRINT",FACE,{"disambiguationData":[TD([[makeQuery(id+"F16.imprint","IMPRINT",EDGE,{"derivedFrom":makeQuery(id+"F1.opExtrude","CAP_EDGE",EDGE,{"disambiguationData":[OSD([sQuery(id+"F0.wireOp",EDGE,"E1.left")])],"isStart":true})}),-1.0]])]});
            var Q3;
            Q3=makeQuery(id+"F2.opExtrude","CAP_FACE",FACE,{"disambiguationData":[OSD([sQuery(id+"F0.wireOp",EDGE,"E12"),sQuery(id+"F0.wireOp",EDGE,"E13"),sQuery(id+"F0.wireOp",EDGE,"E14"),sQuery(id+"F0.wireOp",EDGE,"E15"),sQuery(id+"F0.wireOp",EDGE,"E17.filletArc"),sQuery(id+"F0.wireOp",EDGE,"E18.filletArc"),sQuery(id+"F0.wireOp",EDGE,"E19.filletArc"),sQuery(id+"F0.wireOp",EDGE,"E20.filletArc"),sQuery(id+"F0.wireOp",EDGE,"E25.0"),sQuery(id+"F0.wireOp",EDGE,"E25.1"),sQuery(id+"F0.wireOp",EDGE,"E25.2"),sQuery(id+"F0.wireOp",EDGE,"E25.3"),sQuery(id+"F0.wireOp",EDGE,"E25.4"),sQuery(id+"F0.wireOp",EDGE,"E25.5"),sQuery(id+"F0.wireOp",EDGE,"E25.6"),sQuery(id+"F0.wireOp",EDGE,"E25.7")])],"isStart":false});
            extrude(context, id + "F17", {"entities" : qUnion([Q0, Q1, Q2]), "operationType" : NewBodyOperationType.ADD, "endBound" : BoundingType.UP_TO_SURFACE, "endBoundEntityFace" : qUnion([Q3]), "depth" : 25 * mm});
        }
    });
